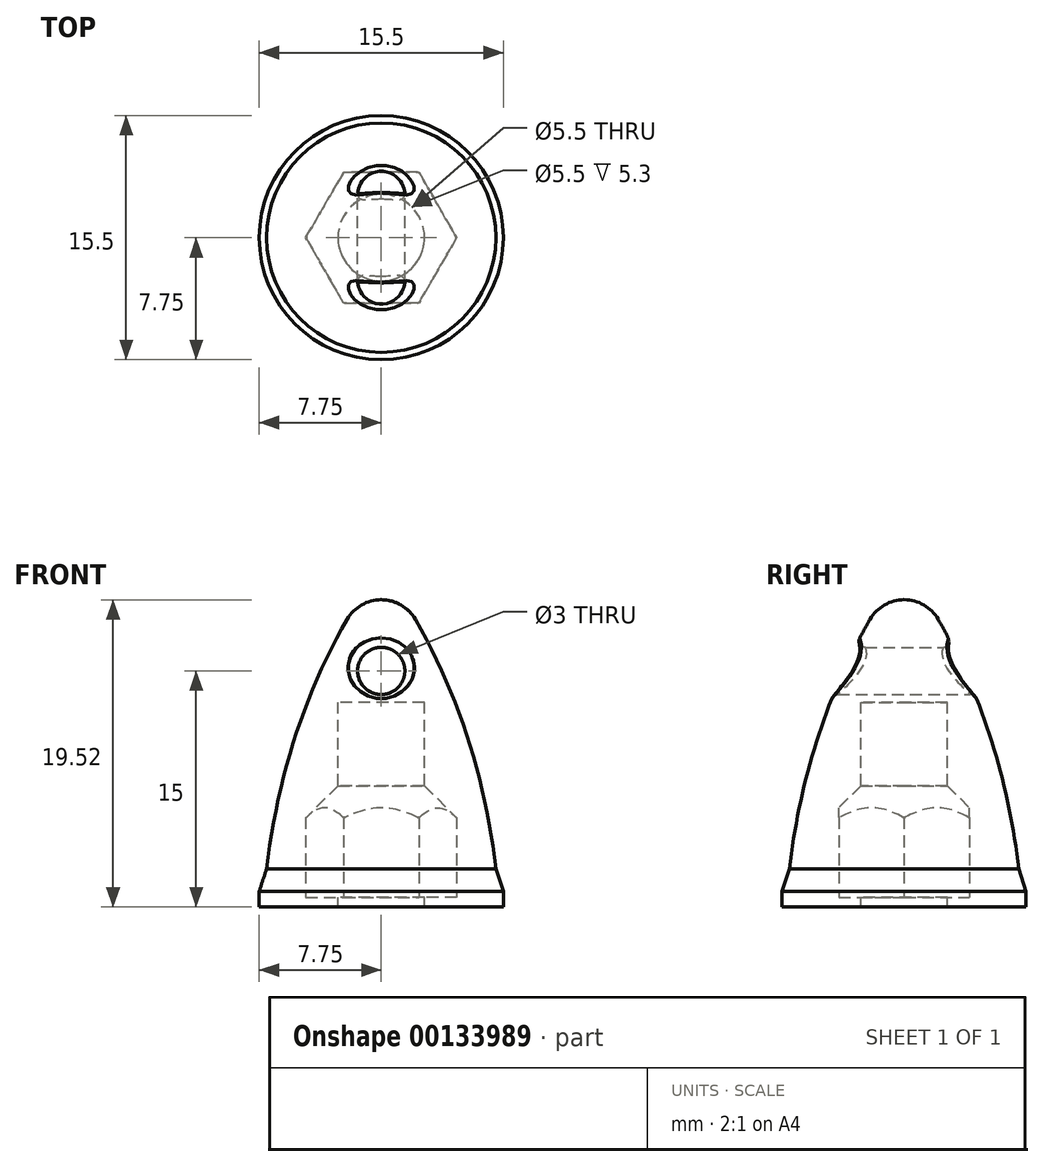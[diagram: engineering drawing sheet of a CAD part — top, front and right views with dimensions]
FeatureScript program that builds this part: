
annotation { "Feature Type Name" : "Feature", "Feature Type Description" : "" }
export const myFeature = defineFeature(function(context is Context, id is Id, definition is map)
    precondition{}
    {
        {
            var Q0;
            Q0=qCreatedBy(makeId("Front.planeOp"),FACE);
            var sketch = newSketch(context, id + "F0", { "sketchPlane" : qUnion([Q0])});
            skLineSegment(sketch, "E0", {"start": v(0, 0) * mm, "end": v(0, 20) * mm, "construction": true});
            skLineSegment(sketch, "E1", {"start": v(0, 0) * mm, "end": v(7.5, 0) * mm, "construction": true});
            skLineSegment(sketch, "E2", {"start": v(0, 0) * mm, "end": v(-7.5, 0) * mm});
            skLineSegment(sketch, "E3.MirrorCS", {"start": v(0, 0) * mm, "end": v(7.5, 0) * mm});
            skEllipticalArc(sketch, "E4.trimOffspring", {});
            skPoint(sketch, "E5.orphan", {"position": v(17.49, 0) * mm});
            skPoint(sketch, "E6.visualSharp", {"position": v(0, 21.56) * mm});
            skCircle(sketch, "E7", {"center": v(0, 15) * mm, "radius": 1.5 * mm});
            skLineSegment(sketch, "E8", {"start": v(0, 15) * mm, "end": v(0, 0) * mm, "construction": true});
            skLineSegment(sketch, "E9", {"start": v(0, 0) * mm, "end": v(0, 20) * mm});
            skLineSegment(sketch, "E10", {"start": v(0, 21.56) * mm, "end": v(0, 21.56) * mm});
            skEllipticalArc(sketch, "E11.MirrorCS", {});
            skArc(sketch, "E12.filletArc", {"start": v(2.16, 18.28) * mm, "mid": v(0, 19.52) * mm, "end": v(-2.16, 18.28) * mm});
            skLineSegment(sketch, "E13", {"start": v(-7.75, 0) * mm, "end": v(-7.75, 1) * mm});
            skLineSegment(sketch, "E14", {"start": v(-7.75, 1) * mm, "end": v(-7.28, 2.43) * mm});
            skLineSegment(sketch, "E15", {"start": v(-7.75, 0) * mm, "end": v(-7.5, 0) * mm});
            const initialGuessF0  = {"E4.trimOffspring": [0.017618327035672555, -0.0019530250337234426, 0.04213860992289035, 0.9991117743044402, 0.03373254959745807, 0.025187138200687447, 0.9588673905191429, 1.4720520455956387], "E11.MirrorCS": [-0.017618327035672555, -0.0019530250337234426, -0.04213860992289035, 0.9991117743044402, 0.03373254959745807, 0.025187138200687447, 4.738860243715008, 5.324317916660459]};
            skSetInitialGuess(sketch, initialGuessF0);
            skSolve(sketch);
        }
        {
            var Q0;
            {var subQ1=sQuery(id+"F0.wireOp",EDGE,"E2");Q0=makeQuery(id+"F0.imprint","IMPRINT",FACE,{"disambiguationData":[TD([[makeQuery(id+"F0.imprint","IMPRINT",EDGE,{"derivedFrom":subQ1}),-1.0]])]});}
            var Q1;
            Q1=sQuery(id+"F0.wireOp",EDGE,"E9");
            revolve(context, id + "F1", {"entities" : qUnion([Q0]), "axis" : qUnion([Q1]), "revolveType" : RevolveType.FULL});
        }
        {
            var Q0;
            {var subQ0=sQuery(id+"F0.wireOp",EDGE,"E9");var subQ1=sQuery(id+"F0.wireOp",EDGE,"E7");var subQ2=makeQuery(id+"F0.imprint","INTERSECT",VERTEX,{"disambiguationData":[OD(0.0)],"derivedFrom":[subQ1,subQ0]});Q0=makeQuery(id+"F0.imprint","IMPRINT",FACE,{"disambiguationData":[TD([[makeQuery(id+"F0.imprint","IMPRINT",EDGE,{"disambiguationData":[TD([[subQ2,1.0]])],"derivedFrom":subQ1}),1.0]])]});}
            var Q1;
            {var subQ0=sQuery(id+"F0.wireOp",EDGE,"E9");var subQ1=sQuery(id+"F0.wireOp",EDGE,"E7");var subQ2=makeQuery(id+"F0.imprint","INTERSECT",VERTEX,{"disambiguationData":[OD(0.0)],"derivedFrom":[subQ1,subQ0]});Q1=makeQuery(id+"F0.imprint","IMPRINT",FACE,{"disambiguationData":[TD([[makeQuery(id+"F0.imprint","IMPRINT",EDGE,{"disambiguationData":[TD([[subQ2,-1.0]])],"derivedFrom":subQ1}),1.0]])]});}
            extrude(context, id + "F2", {"entities" : qUnion([Q0, Q1]), "operationType" : NewBodyOperationType.REMOVE, "endBound" : BoundingType.SYMMETRIC, "depth" : 25 * mm});
        }
        {
            var Q0;
            Q0=qCreatedBy(makeId("Top.planeOp"),FACE);
            cPlane(context, id + "F3", {"entities" : qUnion([Q0]), "cplaneType" : CPlaneType.OFFSET, "offset" : 0.6 * mm, "width" : 150 * mm, "height" : 150 * mm});
        }
        {
            var Q0;
            Q0=qCreatedBy(id+"F3.planeOp",FACE);
            var sketch = newSketch(context, id + "F4", { "sketchPlane" : qUnion([Q0])});
            skCircle(sketch, "E16", {"center": v(0, 0) * mm, "radius": 2.75 * mm});
            skCircle(sketch, "E17.cCircle", {"center": v(0, 0) * mm, "radius": 4.15 * mm, "construction": true});
            skLineSegment(sketch, "E17.0", {"start": v(-2.4, 4.15) * mm, "end": v(2.4, 4.15) * mm});
            skLineSegment(sketch, "E17.1", {"start": v(2.4, 4.15) * mm, "end": v(4.8, 0) * mm});
            skLineSegment(sketch, "E17.2", {"start": v(4.8, 0) * mm, "end": v(2.4, -4.15) * mm});
            skLineSegment(sketch, "E17.3", {"start": v(2.4, -4.15) * mm, "end": v(-2.4, -4.15) * mm});
            skLineSegment(sketch, "E17.4", {"start": v(-2.4, -4.15) * mm, "end": v(-4.8, 0) * mm});
            skLineSegment(sketch, "E17.5", {"start": v(-4.8, 0) * mm, "end": v(-2.4, 4.15) * mm});
            skPoint(sketch, "E17.0.midPoint", {"position": v(0, 4.15) * mm});
            skSolve(sketch);
        }
        {
            var Q0;
            Q0=makeQuery(id+"F4.imprint","IMPRINT",FACE,{"disambiguationData":[TD([[makeQuery(id+"F4.imprint","IMPRINT",EDGE,{"derivedFrom":sQuery(id+"F4.wireOp",EDGE,"E16")}),-1.0]])]});
            var Q1;
            Q1=makeQuery(id+"F4.imprint","IMPRINT",FACE,{"disambiguationData":[TD([[makeQuery(id+"F4.imprint","IMPRINT",EDGE,{"derivedFrom":sQuery(id+"F4.wireOp",EDGE,"E16")}),1.0]])]});
            extrude(context, id + "F5", {"entities" : qUnion([Q0, Q1]), "operationType" : NewBodyOperationType.REMOVE, "depth" : 5.1 * mm});
        }
        {
            var Q0;
            Q0=makeQuery(id+"F4.imprint","IMPRINT",FACE,{"disambiguationData":[TD([[makeQuery(id+"F4.imprint","IMPRINT",EDGE,{"derivedFrom":sQuery(id+"F4.wireOp",EDGE,"E16")}),1.0]])]});
            extrude(context, id + "F6", {"entities" : qUnion([Q0]), "operationType" : NewBodyOperationType.REMOVE, "endBound" : BoundingType.SYMMETRIC, "oppositeDirection" : true, "depth" : 24.8 * mm});
        }
        {
            var Q0;
            Q0=makeQuery(id+"F2.boolean.opBoolean","INTERSECT",EDGE,{"disambiguationData":[OD(0.0)],"derivedFrom":[makeQuery(id+"F1.opRevolve","SWEPT_FACE",FACE,{"disambiguationData":[OSD([sQuery(id+"F0.wireOp",EDGE,"E4.trimOffspring")])]}),makeQuery(id+"F2.opExtrude","SWEPT_FACE",FACE,{"disambiguationData":[OSD([sQuery(id+"F0.wireOp",EDGE,"E7")])]})]});
            var Q1;
            Q1=makeQuery(id+"F2.boolean.opBoolean","INTERSECT",EDGE,{"disambiguationData":[OD(1.0)],"derivedFrom":[makeQuery(id+"F1.opRevolve","SWEPT_FACE",FACE,{"disambiguationData":[OSD([sQuery(id+"F0.wireOp",EDGE,"E4.trimOffspring")])]}),makeQuery(id+"F2.opExtrude","SWEPT_FACE",FACE,{"disambiguationData":[OSD([sQuery(id+"F0.wireOp",EDGE,"E7")])]})]});
            fillet(context, id + "F7", {"entities" : qUnion([Q0, Q1]), "radius" : 0.4 * mm, "tangentPropagation" : true, "allowEdgeOverflow" : false});
        }
        {
            var Q0;
            Q0=makeQuery(id+"F6.boolean.opBoolean","INTERSECT",EDGE,{"derivedFrom":[makeQuery(id+"F5.boolean.opBoolean","COPY",FACE,{"derivedFrom":makeQuery(id+"F5.opExtrude","CAP_FACE",FACE,{"disambiguationData":[OSD([sQuery(id+"F4.wireOp",EDGE,"E17.0"),sQuery(id+"F4.wireOp",EDGE,"E17.1"),sQuery(id+"F4.wireOp",EDGE,"E17.2"),sQuery(id+"F4.wireOp",EDGE,"E17.3"),sQuery(id+"F4.wireOp",EDGE,"E17.4"),sQuery(id+"F4.wireOp",EDGE,"E17.5")])],"isStart":false})}),makeQuery(id+"F6.opExtrude","SWEPT_FACE",FACE,{"disambiguationData":[OSD([sQuery(id+"F4.wireOp",EDGE,"E16")])]})]});
            chamfer(context, id + "F8", {"entities" : qUnion([Q0]), "chamferType" : ChamferType.TWO_OFFSETS, "width1" : 2 * mm, "oppositeDirection" : false, "width2" : 2 * mm, "tangentPropagation" : true});
        }
    });
